# Revit family: Atdec-Bracket-TH-VWV-
name_source: partatom
category: Generic Models
revit_build: Autodesk Revit 2016 (Build: 20150220_1215(x64)
units: mm (PartAtom-declared; Revit-internal decimal feet)

## family parameters
Can host rebar = No
Cut with Voids When Loaded = No
Host = Face
Part Type = Normal
Room Calculation Point = No
Round Connector Dimension = Use Diameter
Shared = No

## types (1)
- TH-VWV
    Assembly Code = E1010800
    Colour Options = Black
    Default Elevation = 1219 mm
    Description = Video wall brackets (set of 2)
    Flat screen maximum supported weight = 165kg (363lb)
    Manufacturer = Atdec
    Master Carton Dimensions = 560mm (20.5") Lenght, 294mm (10.6") Width, 154mm (6.3") Height
    Material = Steel
    Maximum distance from wall (mm) = 44.5mm (1.75")
    Minimum distance from wall (mm) = 44.5mm (1.75")
    Model = TH-VWV
    Pan Adjustment = -
    Product Family = Wall Mount Rail
    Product Information Link = https://www.atdec.com.au
    Range of Motion = Fixed Angle
    Security feature = Can be secured with padlock (not included)
    Single Unit Dimensions = 544mm (19.3") Lenght, 133mm (5.1") Width, 61mm (2.8") Height
    Single units per master pack = 4
    Tilt Adjustment = -
    UPC Code = 881493008335
    URL = www.atdec.com.au
    Universal Height (mm) = From 100 to 400
    Universal Width (mm) = Flexible
    VESA mounting hole pattern,mm = -
    Warranty = 10 years
    Weight, Master Carton = 12.5kg (27.5lb)
    Weight, Single Unit = 3kg (6.6lb)

## geometry (parser evidence)
native form markers: Sweep x2
no freeform markers — native parametric forms only
